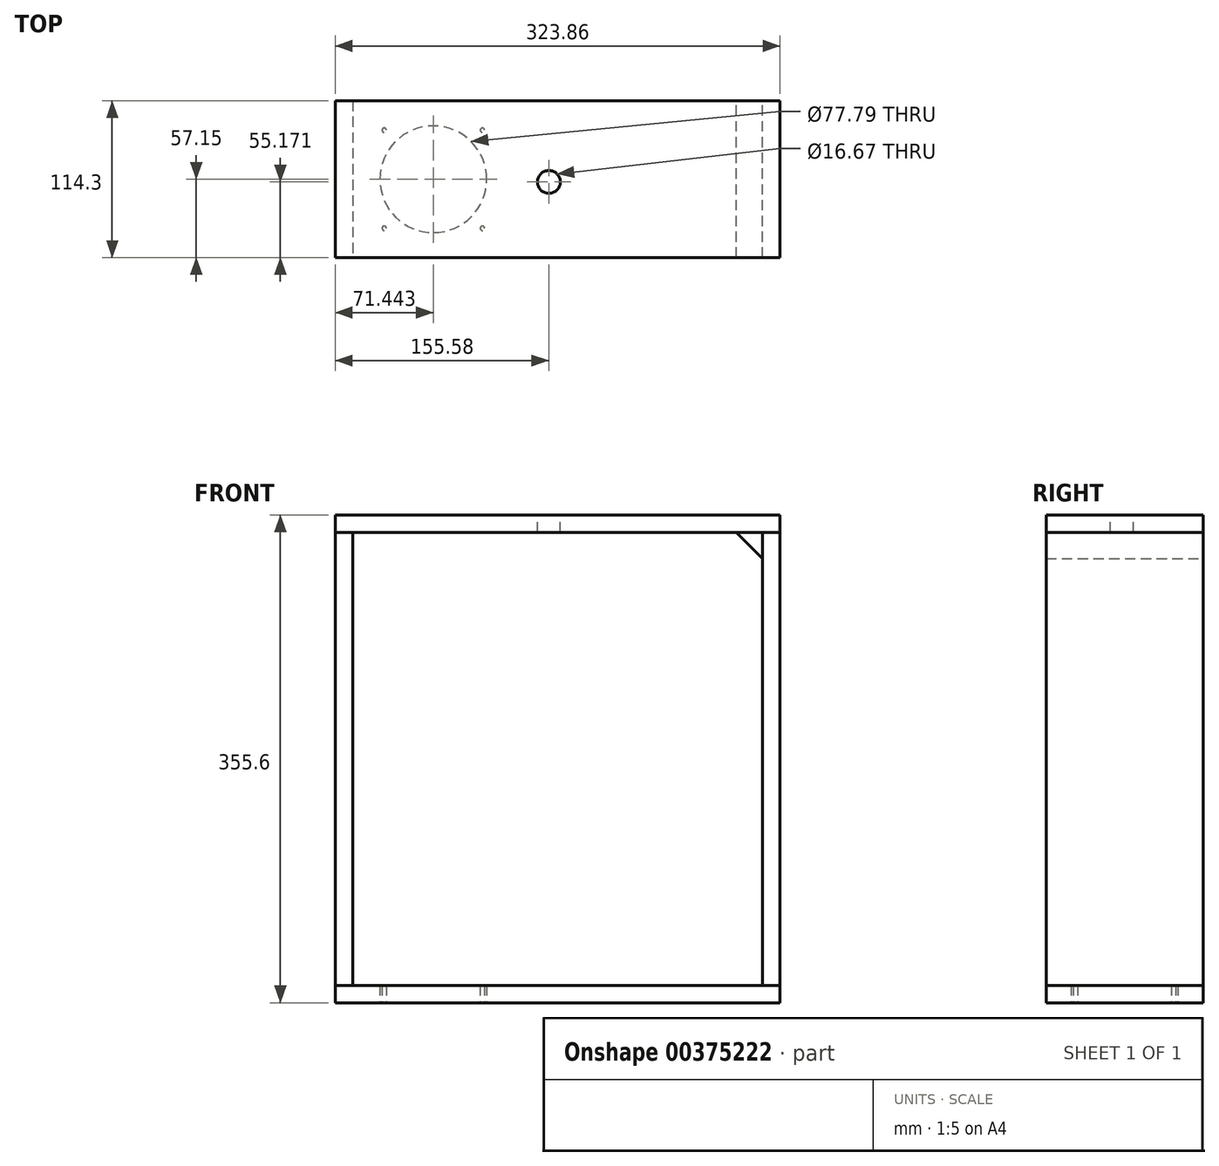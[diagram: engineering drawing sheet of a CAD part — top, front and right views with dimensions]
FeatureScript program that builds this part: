
annotation { "Feature Type Name" : "Feature", "Feature Type Description" : "" }
export const myFeature = defineFeature(function(context is Context, id is Id, definition is map)
    precondition{}
    {
        {
            var Q0;
            Q0=qCreatedBy(makeId("Top.planeOp"),FACE);
            var sketch = newSketch(context, id + "F0", { "sketchPlane" : qUnion([Q0])});
            skLineSegment(sketch, "E0.bottom", {"start": v(161.93, -57.15) * mm, "end": v(-161.93, -57.15) * mm});
            skLineSegment(sketch, "E0.top", {"start": v(161.93, 57.15) * mm, "end": v(-161.93, 57.15) * mm});
            skLineSegment(sketch, "E0.left", {"start": v(161.93, -57.15) * mm, "end": v(161.93, 57.15) * mm});
            skLineSegment(sketch, "E0.right", {"start": v(-161.93, -57.15) * mm, "end": v(-161.93, 57.15) * mm});
            skPoint(sketch, "E0.middle", {"position": v(0, 0) * mm});
            skSolve(sketch);
        }
        {
            var Q0;
            Q0=qSketchRegion(id+"F0",true);
            extrude(context, id + "F1", {"entities" : qUnion([Q0]), "depth" : 12.7 * mm});
        }
        {
            var Q0;
            Q0=makeQuery(id+"F1.opExtrude","SWEPT_FACE",FACE,{"disambiguationData":[OSD([sQuery(id+"F0.wireOp",EDGE,"E0.left")])]});
            var sketch = newSketch(context, id + "F2", { "sketchPlane" : qUnion([Q0])});
            skLineSegment(sketch, "E1.bottom", {"start": v(57.15, 0) * mm, "end": v(-57.15, 0) * mm});
            skLineSegment(sketch, "E1.top", {"start": v(57.15, -330.2) * mm, "end": v(-57.15, -330.2) * mm});
            skLineSegment(sketch, "E1.left", {"start": v(57.15, 0) * mm, "end": v(57.15, -330.2) * mm});
            skLineSegment(sketch, "E1.right", {"start": v(-57.15, 0) * mm, "end": v(-57.15, -330.2) * mm});
            skSolve(sketch);
        }
        {
            var Q0;
            Q0=qSketchRegion(id+"F2",true);
            extrude(context, id + "F3", {"entities" : qUnion([Q0]), "oppositeDirection" : true, "depth" : 12.7 * mm});
        }
        {
            var Q0;
            Q0=makeQuery(id+"F1.opExtrude","SWEPT_FACE",FACE,{"disambiguationData":[OSD([sQuery(id+"F0.wireOp",EDGE,"E0.right")])]});
            var sketch = newSketch(context, id + "F4", { "sketchPlane" : qUnion([Q0])});
            skLineSegment(sketch, "E2.0", {"start": v(-57.15, -330.2) * mm, "end": v(57.15, -330.2) * mm});
            skLineSegment(sketch, "E3", {"start": v(57.15, -330.2) * mm, "end": v(57.15, 0) * mm});
            skLineSegment(sketch, "E4", {"start": v(57.15, 0) * mm, "end": v(-57.15, 0) * mm});
            skLineSegment(sketch, "E5", {"start": v(-57.15, 0) * mm, "end": v(-57.15, -330.2) * mm});
            skSolve(sketch);
        }
        {
            var Q0;
            Q0=qSketchRegion(id+"F4",true);
            extrude(context, id + "F5", {"entities" : qUnion([Q0]), "oppositeDirection" : true, "depth" : 12.7 * mm});
        }
        {
            var Q0;
            Q0=makeQuery(id+"F1.opExtrude","SWEPT_FACE",FACE,{"disambiguationData":[OSD([sQuery(id+"F0.wireOp",EDGE,"E0.top")])]});
            var sketch = newSketch(context, id + "F6", { "sketchPlane" : qUnion([Q0])});
            skPoint(sketch, "E6.0", {"position": v(-149.23, 0) * mm});
            skLineSegment(sketch, "E7", {"start": v(-149.23, 0) * mm, "end": v(-130.18, 0) * mm});
            skLineSegment(sketch, "E8", {"start": v(-130.18, 0) * mm, "end": v(-149.23, -19.05) * mm});
            skLineSegment(sketch, "E9", {"start": v(-149.23, -19.05) * mm, "end": v(-149.23, 0) * mm});
            skSolve(sketch);
        }
        {
            var Q0;
            Q0=qSketchRegion(id+"F6",true);
            var Q1;
            Q1=makeQuery(id+"F1.opExtrude","SWEPT_FACE",FACE,{"disambiguationData":[OSD([sQuery(id+"F0.wireOp",EDGE,"E0.bottom")])]});
            extrude(context, id + "F7", {"entities" : qUnion([Q0]), "endBound" : BoundingType.UP_TO_SURFACE, "oppositeDirection" : true, "endBoundEntityFace" : qUnion([Q1]), "depth" : 25.4 * mm});
        }
        {
            var Q0;
            Q0=makeQuery(id+"F3.opExtrude","SWEPT_FACE",FACE,{"disambiguationData":[OSD([sQuery(id+"F2.wireOp",EDGE,"E1.top")])]});
            var sketch = newSketch(context, id + "F8", { "sketchPlane" : qUnion([Q0])});
            skPoint(sketch, "E10.0", {"position": v(-161.93, 57.15) * mm});
            skLineSegment(sketch, "E11.bottom", {"start": v(161.93, -57.15) * mm, "end": v(-161.93, -57.15) * mm});
            skLineSegment(sketch, "E11.top", {"start": v(161.93, 57.15) * mm, "end": v(-161.93, 57.15) * mm});
            skLineSegment(sketch, "E11.left", {"start": v(161.93, -57.15) * mm, "end": v(161.93, 57.15) * mm});
            skLineSegment(sketch, "E11.right", {"start": v(-161.93, -57.15) * mm, "end": v(-161.93, 57.15) * mm});
            skSolve(sketch);
        }
        {
            var Q0;
            Q0 = qSketchRegion(id + "F8", true);
            extrude(context, id + "F9", {"entities" : qUnion([Q0]), "depth" : 12.7 * mm});
        }
        {
            var Q0;
            Q0=makeQuery(id+"F1.opExtrude","CAP_FACE",FACE,{"disambiguationData":[OSD([sQuery(id+"F0.wireOp",EDGE,"E0.bottom"),sQuery(id+"F0.wireOp",EDGE,"E0.top"),sQuery(id+"F0.wireOp",EDGE,"E0.left"),sQuery(id+"F0.wireOp",EDGE,"E0.right")])],"isStart":false});
            var sketch = newSketch(context, id + "F10", { "sketchPlane" : qUnion([Q0])});
            skPoint(sketch, "E12", {"position": v(-6.35, -1.98) * mm});
            skSolve(sketch);
        }
        {
            var Q0;
            Q0=sQuery(id+"F10.wireOp",VERTEX,"E12");
            var Q1;
            Q1=makeQuery(id+"F1.opExtrude","SWEPT_BODY",BODY,{"disambiguationData":[OSD([sQuery(id+"F0.wireOp",EDGE,"E0.bottom"),sQuery(id+"F0.wireOp",EDGE,"E0.top"),sQuery(id+"F0.wireOp",EDGE,"E0.left"),sQuery(id+"F0.wireOp",EDGE,"E0.right")])]});
            hole(context, id + "F11", {"style" : HoleStyle.SIMPLE, "endStyle" : HoleEndStyle.THROUGH, "holeDiameter" : 16.67 * mm, "isTappedThrough" : true, "tappedDepth" : 12.7 * mm, "tapClearance" : 3, "locations" : qUnion([Q0]), "scope" : qUnion([Q1])});
        }
        {
            var Q0;
            Q0=makeQuery(id+"F9.opExtrude","CAP_FACE",FACE,{"disambiguationData":[OSD([sQuery(id+"F8.wireOp",EDGE,"E11.bottom"),sQuery(id+"F8.wireOp",EDGE,"E11.top"),sQuery(id+"F8.wireOp",EDGE,"E11.left"),sQuery(id+"F8.wireOp",EDGE,"E11.right")])],"isStart":false});
            var sketch = newSketch(context, id + "F12", { "sketchPlane" : qUnion([Q0])});
            skPoint(sketch, "E13", {"position": v(-90.49, 0) * mm});
            skSolve(sketch);
        }
        {
            var Q0;
            Q0=sQuery(id+"F12.wireOp",VERTEX,"E13");
            var Q1;
            Q1=makeQuery(id+"F9.opExtrude","SWEPT_BODY",BODY,{"disambiguationData":[OSD([sQuery(id+"F8.wireOp",EDGE,"E11.bottom"),sQuery(id+"F8.wireOp",EDGE,"E11.top"),sQuery(id+"F8.wireOp",EDGE,"E11.left"),sQuery(id+"F8.wireOp",EDGE,"E11.right")])]});
            hole(context, id + "F13", {"style" : HoleStyle.SIMPLE, "endStyle" : HoleEndStyle.THROUGH, "holeDiameter" : 77.8 * mm, "isTappedThrough" : true, "tappedDepth" : 12.7 * mm, "tapClearance" : 3, "locations" : qUnion([Q0]), "scope" : qUnion([Q1])});
        }
        {
            var Q0;
            Q0=makeQuery(id+"F9.opExtrude","CAP_FACE",FACE,{"disambiguationData":[OSD([sQuery(id+"F8.wireOp",EDGE,"E11.bottom"),sQuery(id+"F8.wireOp",EDGE,"E11.top"),sQuery(id+"F8.wireOp",EDGE,"E11.left"),sQuery(id+"F8.wireOp",EDGE,"E11.right")])],"isStart":false});
            var sketch = newSketch(context, id + "F14", { "sketchPlane" : qUnion([Q0])});
            skCircle(sketch, "E14.0", {"center": v(-90.49, 0) * mm, "radius": 38.9 * mm, "construction": true});
            skPoint(sketch, "E15", {"position": v(-54.74, 35.75) * mm});
            skPoint(sketch, "E16", {"position": v(-54.74, -35.75) * mm});
            skPoint(sketch, "E17", {"position": v(-126.24, -35.75) * mm});
            skPoint(sketch, "E18", {"position": v(-126.24, 35.75) * mm});
            skLineSegment(sketch, "E19", {"start": v(-90.49, 0) * mm, "end": v(9.5, 0) * mm, "construction": true});
            skLineSegment(sketch, "E20", {"start": v(-90.49, 0) * mm, "end": v(-90.49, -89.82) * mm, "construction": true});
            skSolve(sketch);
        }
        {
            var Q0;
            Q0=sQuery(id+"F14.wireOp",VERTEX,"E15");
            var Q1;
            Q1=sQuery(id+"F14.wireOp",VERTEX,"E18");
            var Q2;
            Q2=sQuery(id+"F14.wireOp",VERTEX,"E17");
            var Q3;
            Q3=sQuery(id+"F14.wireOp",VERTEX,"E16");
            var Q4;
            Q4=makeQuery(id+"F9.opExtrude","SWEPT_BODY",BODY,{"disambiguationData":[OSD([sQuery(id+"F8.wireOp",EDGE,"E11.bottom"),sQuery(id+"F8.wireOp",EDGE,"E11.top"),sQuery(id+"F8.wireOp",EDGE,"E11.left"),sQuery(id+"F8.wireOp",EDGE,"E11.right")])]});
            hole(context, id + "F15", {"style" : HoleStyle.SIMPLE, "endStyle" : HoleEndStyle.THROUGH, "holeDiameter" : 3.17 * mm, "isTappedThrough" : true, "tappedDepth" : 12.7 * mm, "tapClearance" : 3, "locations" : qUnion([Q0, Q1, Q2, Q3]), "scope" : qUnion([Q4])});
        }
    });
